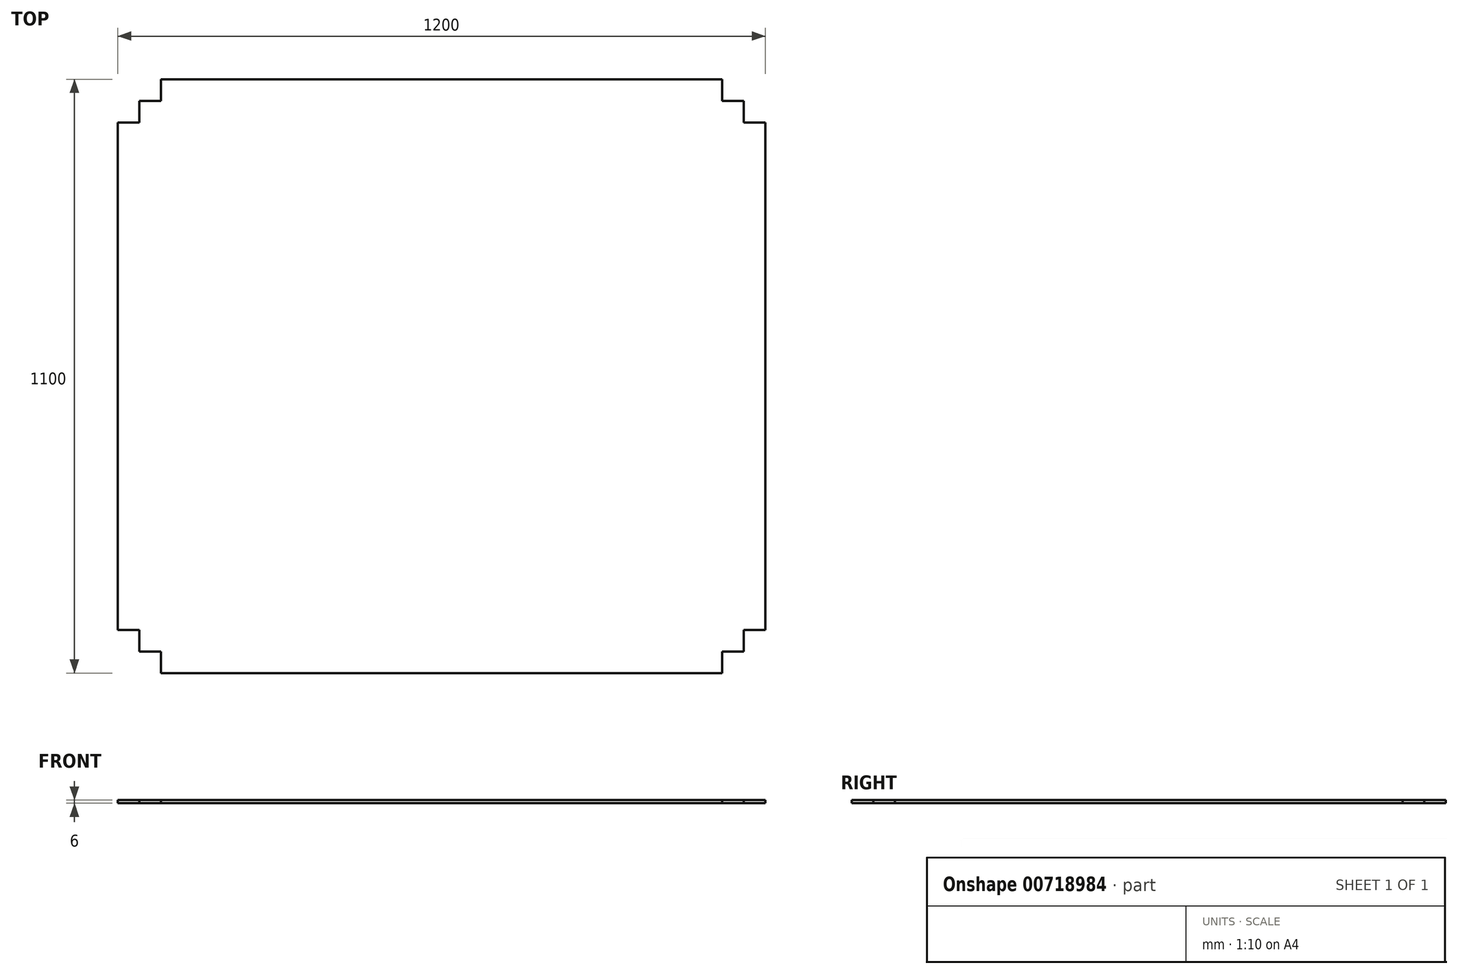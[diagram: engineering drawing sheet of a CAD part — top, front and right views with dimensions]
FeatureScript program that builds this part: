
annotation { "Feature Type Name" : "Feature", "Feature Type Description" : "" }
export const myFeature = defineFeature(function(context is Context, id is Id, definition is map)
    precondition{}
    {
        {
            var Q0;
            Q0=qCreatedBy(makeId("Top.planeOp"),FACE);
            var sketch = newSketch(context, id + "F0", { "sketchPlane" : qUnion([Q0])});
            skLineSegment(sketch, "E0", {"start": v(-520, 550) * mm, "end": v(-520, 510) * mm});
            skLineSegment(sketch, "E1", {"start": v(-520, 510) * mm, "end": v(-560, 510) * mm});
            skLineSegment(sketch, "E2", {"start": v(-560, 510) * mm, "end": v(-560, 470) * mm});
            skLineSegment(sketch, "E3", {"start": v(-560, 470) * mm, "end": v(-600, 470) * mm});
            skLineSegment(sketch, "E4", {"start": v(-600, 470) * mm, "end": v(-600, -470) * mm});
            skLineSegment(sketch, "E5", {"start": v(-600, -470) * mm, "end": v(-560, -470) * mm});
            skLineSegment(sketch, "E6", {"start": v(-560, -470) * mm, "end": v(-560, -510) * mm});
            skLineSegment(sketch, "E7", {"start": v(-560, -510) * mm, "end": v(-520, -510) * mm});
            skLineSegment(sketch, "E8", {"start": v(-520, -510) * mm, "end": v(-520, -550) * mm});
            skLineSegment(sketch, "E9", {"start": v(-520, -550) * mm, "end": v(520, -550) * mm});
            skLineSegment(sketch, "E10", {"start": v(520, -550) * mm, "end": v(520, -510) * mm});
            skLineSegment(sketch, "E11", {"start": v(520, -510) * mm, "end": v(560, -510) * mm});
            skLineSegment(sketch, "E12", {"start": v(560, -510) * mm, "end": v(560, -470) * mm});
            skLineSegment(sketch, "E13", {"start": v(560, -470) * mm, "end": v(600, -470) * mm});
            skLineSegment(sketch, "E14", {"start": v(600, -470) * mm, "end": v(600, 470) * mm});
            skLineSegment(sketch, "E15", {"start": v(600, 470) * mm, "end": v(560, 470) * mm});
            skLineSegment(sketch, "E16", {"start": v(560, 470) * mm, "end": v(560, 510) * mm});
            skLineSegment(sketch, "E17", {"start": v(560, 510) * mm, "end": v(520, 510) * mm});
            skLineSegment(sketch, "E18", {"start": v(520, 510) * mm, "end": v(520, 550) * mm});
            skLineSegment(sketch, "E19", {"start": v(520, 550) * mm, "end": v(-520, 550) * mm});
            skSolve(sketch);
        }
        {
            var Q0;
            Q0=makeQuery(id+"F0.imprint","IMPRINT",FACE,{"disambiguationData":[TD([[makeQuery(id+"F0.imprint","IMPRINT",EDGE,{"derivedFrom":sQuery(id+"F0.wireOp",EDGE,"E0")}),1.0]])]});
            extrude(context, id + "F1", {"entities" : qUnion([Q0]), "depth" : 6 * mm, "offsetDistance" : 25 * mm});
        }
    });
